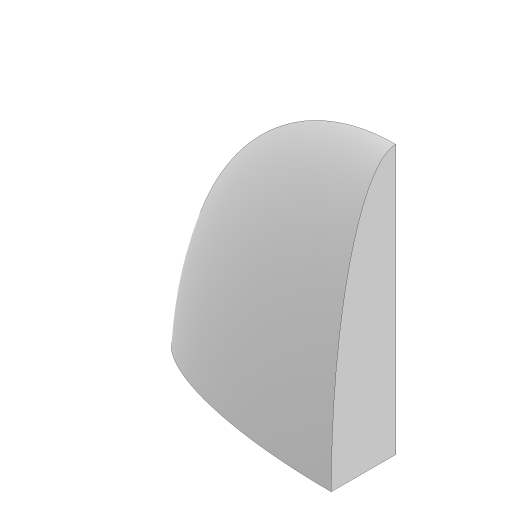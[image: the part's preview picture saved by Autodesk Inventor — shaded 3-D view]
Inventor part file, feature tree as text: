
AUTODESK INVENTOR PART (.ipt)
format: ipt  version: 2023 (Build 270158000, 158)  size: 143,872 bytes
history: native  units: in
note: dims shown in document units (in); Inventor stores cm internally (conversion verified against a paired STEP export)
features: sketch x3, loft x1
ambient origin geometry x8: Origin, YZ Plane, XZ Plane, XY Plane, X Axis, Y Axis, Z Axis, Center Point
bodies: Body1 (feature_tree)
feature tree (4):
  loft  "Loft1"
  sketch  "Sketch1"  dims[d0=49.2126in d1=39.3701in]
  sketch  "Sketch7"  dims[d9=11.811in]
  sketch  "Sketch8"  dims[d10=39.3701in d11=11.811in d12=49.2126in d13=0.0in d14=90.0deg d15=0.0in d16=90.0deg d17=0.0in d18=90.0deg]
